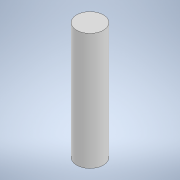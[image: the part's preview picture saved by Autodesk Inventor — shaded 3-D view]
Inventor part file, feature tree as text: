
AUTODESK INVENTOR PART (.ipt)
format: ipt  version: 2021 (Build 250183000, 183)  size: 89,088 bytes
history: native  units: mm
features: extrude x1, sketch x1
ambient origin geometry x8: Origin, YZ Plane, XZ Plane, XY Plane, X Axis, Y Axis, Z Axis, Center Point
bodies: Solid1 (feature_tree)
feature tree (2):
  extrude  "Extrusion1"  Depth=14.0mm TaperAngle=0.0deg
  sketch  "Sketch1"  dims[d0=3.2mm d1=14.0mm d2=0.0mm]
